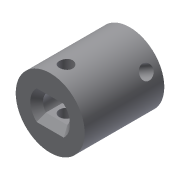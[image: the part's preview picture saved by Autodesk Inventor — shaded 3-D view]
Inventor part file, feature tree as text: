
AUTODESK INVENTOR PART (.ipt)
format: ipt  version: 2019.4 (Build 234330000, 330)  size: 188,416 bytes
history: native  units: mm
features: reference x9, other x5, sketch x4, extrude x4, projected_geometry x3, plane x1, chamfer x1, pattern_circular x1, hole x1
ambient origin geometry x8: Origin, YZ Plane, XZ Plane, XY Plane, X Axis, Y Axis, Z Axis, Center Point
bodies: Solid1 (feature_tree)
feature tree (29):
  sketch  "Sketch1"  dims[d2=10.0mm d3=0.0mm d5=5.0mm d6=0.0mm]
  plane  "Work Plane1"
  extrude  "Extrusion1"  Depth=10.0mm TaperAngle=0.0deg
  extrude  "Extrusion2"  Depth=5.4mm
  chamfer  "Chamfer1"  Distance=13.0mm
  extrude  "Extrusion3"  Depth=10.0mm
  pattern_circular  "Circular Pattern1"  [2 undecoded]
  hole  "Hole1"  [1 undecoded]
  extrude  "Extrusion4"  Depth=10.0mm TaperAngle=360.0deg
  reference  "Reference1"
  reference  "Reference2"
  reference  "Reference3"
  reference  "Reference4"
  sketch  "Sketch2"  dims[d7=1.2mm d8=2.0mm d9=45.0deg d10=5.4mm]
  reference  "Reference5"
  reference  "Reference6"
  reference  "Reference7"
  reference  "Reference8"
  reference  "Reference9"
  sketch  "Sketch3"  dims[d11=3.1mm]
  projected_geometry  "Projected Loop2"
  projected_geometry  "Projected Loop3"
  projected_geometry  "Projected Loop4"
  sketch  "Sketch5"  dims[d12=2.55mm d13=13.0mm d14=2.5mm d15=2.5mm d16=10.0mm d17=0.0mm d18=30.0mm d19=360.0deg d21=2.5mm d22=6.0mm d23=4.0mm d24=2.0mm d25=90.0deg d26=8.0mm d27=20.594885mm d28=3.2mm d29=10.0mm d30=-0.174533mm]
  other  "Assembly_XY_Translator_Lightsheet_v2.iam"
  other  "DIN 912 - replaced by DIN EN ISO 4762 M3 x 30:1"
  other  "ANSI B18.2.4.2M M3x0.5:2"
  other  "00_X_Translator_Lightsheet_v4:1"
  other  "28BYJ-48:1"
note: 3 required parameter values undecoded (feature->parameter linkage not recoverable at this tier; creation-order binding heuristic only, values carry confidence <= 0.55)
